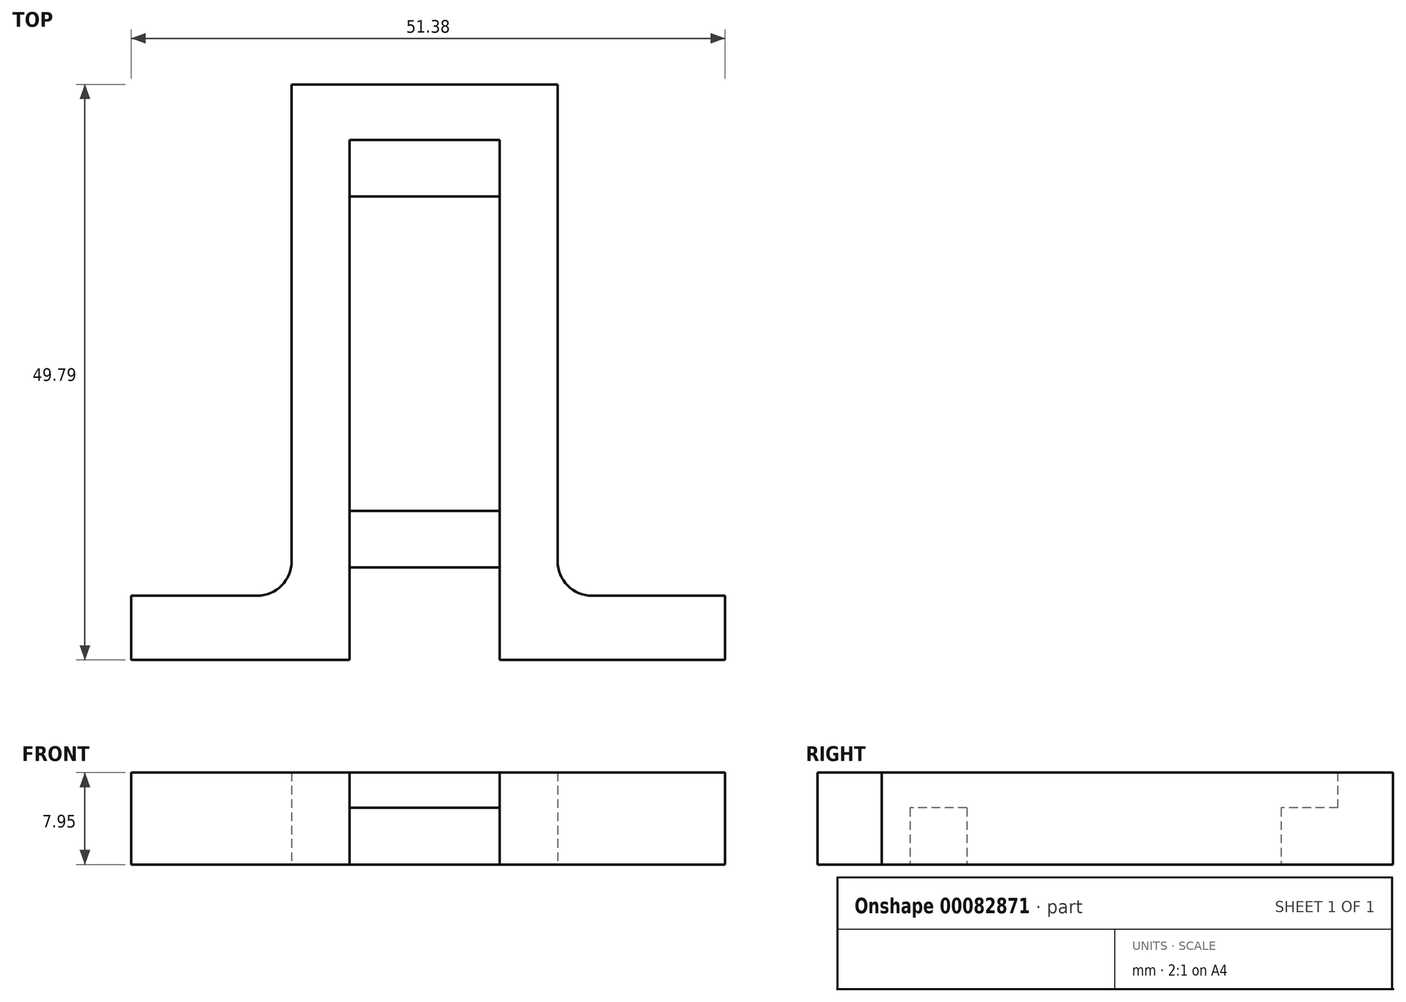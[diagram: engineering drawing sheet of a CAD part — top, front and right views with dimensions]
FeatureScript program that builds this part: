
annotation { "Feature Type Name" : "Feature", "Feature Type Description" : "" }
export const myFeature = defineFeature(function(context is Context, id is Id, definition is map)
    precondition{}
    {
        {
            var Q0;
            Q0=qCreatedBy(makeId("Top.planeOp"),FACE);
            var sketch = newSketch(context, id + "F0", { "sketchPlane" : qUnion([Q0])});
            skLineSegment(sketch, "E0.bottom", {"start": v(11.5, 2.4) * mm, "end": v(-11.5, 2.4) * mm});
            skLineSegment(sketch, "E0.top", {"start": v(11.5, -2.4) * mm, "end": v(-11.5, -2.4) * mm});
            skLineSegment(sketch, "E0.left", {"start": v(11.5, 2.4) * mm, "end": v(11.5, -2.4) * mm});
            skLineSegment(sketch, "E0.right", {"start": v(-11.5, 2.4) * mm, "end": v(-11.5, -2.4) * mm});
            skPoint(sketch, "E0.middle", {"position": v(0, 0) * mm});
            skLineSegment(sketch, "E1.bottom", {"start": v(11.5, -2.4) * mm, "end": v(6.5, -2.4) * mm});
            skLineSegment(sketch, "E1.top", {"start": v(11.5, -47.39) * mm, "end": v(6.5, -47.39) * mm});
            skLineSegment(sketch, "E1.left", {"start": v(11.5, -2.4) * mm, "end": v(11.5, -47.39) * mm});
            skLineSegment(sketch, "E1.right", {"start": v(6.5, -2.4) * mm, "end": v(6.5, -47.39) * mm});
            skLineSegment(sketch, "E2.bottom", {"start": v(-11.5, -2.4) * mm, "end": v(-6.5, -2.4) * mm});
            skLineSegment(sketch, "E2.top", {"start": v(-11.5, -47.39) * mm, "end": v(-6.5, -47.39) * mm});
            skLineSegment(sketch, "E2.left", {"start": v(-11.5, -2.4) * mm, "end": v(-11.5, -47.39) * mm});
            skLineSegment(sketch, "E2.right", {"start": v(-6.5, -2.4) * mm, "end": v(-6.5, -47.39) * mm});
            skLineSegment(sketch, "E3.bottom", {"start": v(-11.5, -47.39) * mm, "end": v(-25.38, -47.39) * mm});
            skLineSegment(sketch, "E3.top", {"start": v(-11.5, -41.83) * mm, "end": v(-25.38, -41.83) * mm});
            skLineSegment(sketch, "E3.left", {"start": v(-11.5, -47.39) * mm, "end": v(-11.5, -41.83) * mm});
            skLineSegment(sketch, "E3.right", {"start": v(-25.38, -47.39) * mm, "end": v(-25.38, -41.83) * mm});
            skPoint(sketch, "E4.oppositeSnap0", {"position": v(-18.44, -41.83) * mm});
            skLineSegment(sketch, "E4.bottom", {"start": v(11.5, -47.39) * mm, "end": v(26, -47.39) * mm});
            skLineSegment(sketch, "E4.top", {"start": v(11.5, -41.83) * mm, "end": v(26, -41.83) * mm});
            skLineSegment(sketch, "E4.left", {"start": v(11.5, -47.39) * mm, "end": v(11.5, -41.83) * mm});
            skLineSegment(sketch, "E4.right", {"start": v(26, -47.39) * mm, "end": v(26, -41.83) * mm});
            skSolve(sketch);
        }
        {
            var Q0;
            Q0=qSketchRegion(id+"F0",true);
            extrude(context, id + "F1", {"entities" : qUnion([Q0]), "depth" : 7.95 * mm});
        }
        {
            var Q0;
            Q0=makeQuery(id+"F1.opExtrude","CAP_FACE",FACE,{"disambiguationData":[OSD([sQuery(id+"F0.wireOp",EDGE,"E0.bottom"),sQuery(id+"F0.wireOp",EDGE,"E0.top"),sQuery(id+"F0.wireOp",EDGE,"E0.left"),sQuery(id+"F0.wireOp",EDGE,"E0.right"),sQuery(id+"F0.wireOp",EDGE,"E1.top"),sQuery(id+"F0.wireOp",EDGE,"E1.left"),sQuery(id+"F0.wireOp",EDGE,"E1.right"),sQuery(id+"F0.wireOp",EDGE,"E2.top"),sQuery(id+"F0.wireOp",EDGE,"E2.left"),sQuery(id+"F0.wireOp",EDGE,"E2.right"),sQuery(id+"F0.wireOp",EDGE,"E3.bottom"),sQuery(id+"F0.wireOp",EDGE,"E3.top"),sQuery(id+"F0.wireOp",EDGE,"E3.right"),sQuery(id+"F0.wireOp",EDGE,"E4.bottom"),sQuery(id+"F0.wireOp",EDGE,"E4.top"),sQuery(id+"F0.wireOp",EDGE,"E4.right")])],"isStart":true});
            var sketch = newSketch(context, id + "F2", { "sketchPlane" : qUnion([Q0])});
            skLineSegment(sketch, "E5.bottom", {"start": v(-6.5, 34.49) * mm, "end": v(6.5, 34.49) * mm});
            skLineSegment(sketch, "E5.top", {"start": v(-6.5, 39.39) * mm, "end": v(6.5, 39.39) * mm});
            skLineSegment(sketch, "E5.left", {"start": v(-6.5, 34.49) * mm, "end": v(-6.5, 39.39) * mm});
            skLineSegment(sketch, "E5.right", {"start": v(6.5, 34.49) * mm, "end": v(6.5, 39.39) * mm});
            skSolve(sketch);
        }
        {
            var Q0;
            Q0=qSketchRegion(id+"F2",true);
            extrude(context, id + "F3", {"entities" : qUnion([Q0]), "oppositeDirection" : true, "depth" : 4.9 * mm});
        }
        {
            var Q0;
            Q0=qCreatedBy(makeId("Top.planeOp"),FACE);
            var sketch = newSketch(context, id + "F4", { "sketchPlane" : qUnion([Q0])});
            skLineSegment(sketch, "E6.bottom", {"start": v(-6.5, -2.4) * mm, "end": v(6.5, -2.4) * mm});
            skLineSegment(sketch, "E6.top", {"start": v(-6.5, -7.3) * mm, "end": v(6.5, -7.3) * mm});
            skLineSegment(sketch, "E6.left", {"start": v(-6.5, -2.4) * mm, "end": v(-6.5, -7.3) * mm});
            skLineSegment(sketch, "E6.right", {"start": v(6.5, -2.4) * mm, "end": v(6.5, -7.3) * mm});
            skSolve(sketch);
        }
        {
            var Q0;
            Q0=qSketchRegion(id+"F4",true);
            extrude(context, id + "F5", {"entities" : qUnion([Q0]), "operationType" : NewBodyOperationType.ADD, "depth" : 4.9 * mm});
        }
        {
            var Q0;
            Q0=makeQuery(id+"F1.opExtrude","SWEPT_EDGE",EDGE,{"disambiguationData":[OSD([sQuery(id+"F0.wireOp",EDGE,"E2.left"),sQuery(id+"F0.wireOp",EDGE,"E3.top"),sQuery(id+"F0.wireOp",EDGE,"E3.left")])]});
            fillet(context, id + "F6", {"entities" : qUnion([Q0]), "radius" : 3 * mm, "tangentPropagation" : true, "allowEdgeOverflow" : false});
        }
        {
            var Q0;
            Q0=makeQuery(id+"F1.opExtrude","SWEPT_EDGE",EDGE,{"disambiguationData":[OSD([sQuery(id+"F0.wireOp",EDGE,"E1.left"),sQuery(id+"F0.wireOp",EDGE,"E4.top"),sQuery(id+"F0.wireOp",EDGE,"E4.left")])]});
            fillet(context, id + "F7", {"entities" : qUnion([Q0]), "radius" : 3 * mm, "tangentPropagation" : true, "allowEdgeOverflow" : false});
        }
    });
